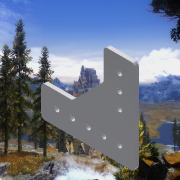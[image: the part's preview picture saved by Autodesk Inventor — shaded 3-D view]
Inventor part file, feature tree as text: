
AUTODESK INVENTOR PART (.ipt)
format: ipt  version: 2015 SP1 (Build 190203100, 203)  size: 183,808 bytes
history: native  units: in
note: dims shown in document units (in); Inventor stores cm internally (conversion verified against a paired STEP export)
features: sketch x2, reference x2, extrude x1, fillet x1, hole x1
ambient origin geometry x8: Origin, YZ Plane, XZ Plane, XY Plane, X Axis, Y Axis, Z Axis, Center Point
bodies: Solid1 (feature_tree)
feature tree (7):
  extrude  "Extrusion1"  Depth=3.0in
  fillet  "Fillet2"  Radius=0.125in
  hole  "Hole1"  [1 undecoded]
  sketch  "Sketch1"  dims[d1=3.0in d2=3.0in d3=0.125in d4=0.0in]
  sketch  "Sketch2"  dims[d7=1.0in d8=1.0in d9=0.125in d10=0.163in d11=0.75in d12=0.375in d13=0.25in d14=0.5635in d15=1.0in d16=0.8108in]
  reference  "Reference2"
  reference  "Reference3"
note: 1 required parameter value undecoded (feature->parameter linkage not recoverable at this tier; creation-order binding heuristic only, values carry confidence <= 0.55)
